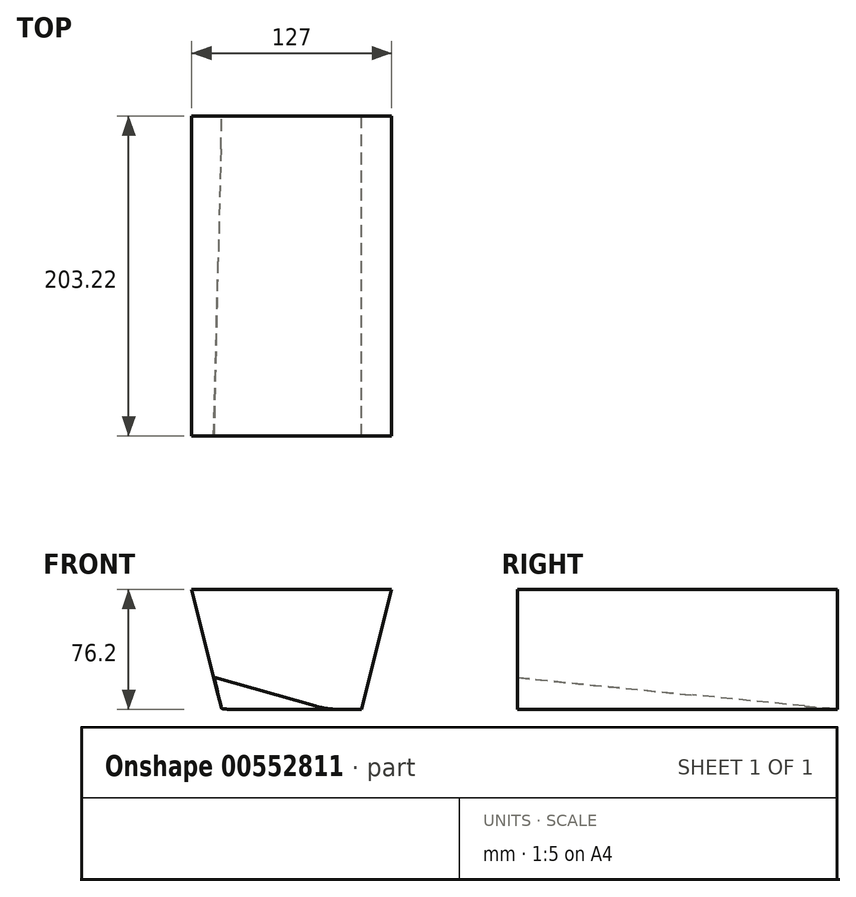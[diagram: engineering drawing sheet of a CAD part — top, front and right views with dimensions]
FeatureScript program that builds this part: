
annotation { "Feature Type Name" : "Feature", "Feature Type Description" : "" }
export const myFeature = defineFeature(function(context is Context, id is Id, definition is map)
    precondition{}
    {
        {
            var Q0;
            Q0=qCreatedBy(makeId("Front.planeOp"),FACE);
            var sketch = newSketch(context, id + "F0", { "sketchPlane" : qUnion([Q0])});
            skLineSegment(sketch, "E0.bottom", {"start": v(63.5, -38.1) * mm, "end": v(-63.5, -38.1) * mm});
            skLineSegment(sketch, "E0.top", {"start": v(63.5, 38.1) * mm, "end": v(-63.5, 38.1) * mm});
            skLineSegment(sketch, "E0.left", {"start": v(63.5, -38.1) * mm, "end": v(63.5, 38.1) * mm});
            skLineSegment(sketch, "E0.right", {"start": v(-63.5, -38.1) * mm, "end": v(-63.5, 38.1) * mm});
            skPoint(sketch, "E0.middle", {"position": v(0, 0) * mm});
            skLineSegment(sketch, "E1", {"start": v(-63.5, 38.1) * mm, "end": v(-44.45, -38.1) * mm});
            skLineSegment(sketch, "E2", {"start": v(0, 38.1) * mm, "end": v(0, -38.1) * mm, "construction": true});
            skLineSegment(sketch, "E3.MirrorCS", {"start": v(63.5, 38.1) * mm, "end": v(44.45, -38.1) * mm});
            skSolve(sketch);
        }
        {
            var Q0;
            Q0=makeQuery(id+"F0.imprint","IMPRINT",FACE,{"disambiguationData":[TD([[makeQuery(id+"F0.imprint","IMPRINT",EDGE,{"derivedFrom":sQuery(id+"F0.wireOp",EDGE,"E0.top")}),1.0]])]});
            extrude(context, id + "F1", {"entities" : qUnion([Q0]), "depth" : 203.2 * mm, "offsetDistance" : 25.4 * mm});
        }
        {
            var Q0;
            Q0=makeQuery(id+"F1.opExtrude","CAP_FACE",FACE,{"disambiguationData":[OSD([sQuery(id+"F0.wireOp",EDGE,"E0.bottom"),sQuery(id+"F0.wireOp",EDGE,"E0.top"),sQuery(id+"F0.wireOp",EDGE,"E1"),sQuery(id+"F0.wireOp",EDGE,"E3.MirrorCS")])],"isStart":false});
            var sketch = newSketch(context, id + "F2", { "sketchPlane" : qUnion([Q0])});
            skLineSegment(sketch, "E4", {"start": v(-49.53, -17.78) * mm, "end": v(-44.45, -38.1) * mm});
            skLineSegment(sketch, "E5", {"start": v(-44.45, -38.1) * mm, "end": v(0, -38.1) * mm});
            skLineSegment(sketch, "E6", {"start": v(0, -38.1) * mm, "end": v(0, -31.75) * mm});
            skLineSegment(sketch, "E7", {"start": v(0, -31.75) * mm, "end": v(-49.53, -17.78) * mm});
            skSolve(sketch);
        }
        {
            var Q0;
            Q0=sQuery(id+"F2.wireOp",VERTEX,"E7.start");
            var Q1;
            Q1=sQuery(id+"F2.wireOp",VERTEX,"E4.start");
            var Q2;
            Q2=makeQuery(id+"F1.opExtrude","CAP_VERTEX",VERTEX,{"disambiguationData":[OSD([sQuery(id+"F0.wireOp",EDGE,"E0.bottom"),sQuery(id+"F0.wireOp",EDGE,"E1")])],"isStart":true});
            cPlane(context, id + "F3", {"entities" : qUnion([Q0, Q1, Q2]), "cplaneType" : CPlaneType.THREE_POINT, "offset" : 25.4 * mm, "width" : 152.4 * mm, "height" : 152.4 * mm});
        }
        {
            var Q0;
            Q0=qCreatedBy(id+"F3.planeOp",FACE);
            var sketch = newSketch(context, id + "F4", { "sketchPlane" : qUnion([Q0])});
            skLineSegment(sketch, "E8", {"start": v(-37.81, -200.68) * mm, "end": v(-32.54, 3.53) * mm});
            skLineSegment(sketch, "E9", {"start": v(-37.81, -200.68) * mm, "end": v(83.29, -203.81) * mm});
            skLineSegment(sketch, "E10", {"start": v(-32.54, 3.53) * mm, "end": v(83.29, 0.53) * mm});
            skLineSegment(sketch, "E11", {"start": v(83.29, 0.53) * mm, "end": v(83.29, -203.81) * mm});
            skSolve(sketch);
        }
        {
            var Q0;
            Q0 = qSketchRegion(id + "F4", true);
            extrude(context, id + "F5", {"entities" : qUnion([Q0]), "operationType" : NewBodyOperationType.REMOVE, "endBound" : BoundingType.THROUGH_ALL, "oppositeDirection" : true, "depth" : 25.4 * mm, "offsetDistance" : 25.4 * mm});
        }
        {
            var Q0;
            {var subQ0=sQuery(id+"F4.wireOp",EDGE,"E11");var subQ1=sQuery(id+"F4.wireOp",EDGE,"E10");var subQ2=sQuery(id+"F4.wireOp",EDGE,"E9");var subQ3=sQuery(id+"F4.wireOp",EDGE,"E8");Q0=makeQuery(id+"F4tuMMxzGeYJKgA_1.1.F5.boolean.opBoolean","INTERSECT",EDGE,{"derivedFrom":[makeQuery(id+"F5.boolean.opBoolean","COPY",FACE,{"derivedFrom":makeQuery(id+"F5.opExtrude","CAP_FACE",FACE,{"disambiguationData":[OSD([subQ3,subQ2,subQ1,subQ0])],"isStart":true})}),makeQuery(id+"F4tuMMxzGeYJKgA_1.1.F5.opExtrude","CAP_FACE",FACE,{"disambiguationData":[OSD([subQ3,subQ2,subQ1,subQ0])],"isStart":true})]});}
            var Q1;
            Q1=makeQuery(id+"F5.boolean.opBoolean","INTERSECT",EDGE,{"derivedFrom":[makeQuery(id+"F1.opExtrude","SWEPT_FACE",FACE,{"disambiguationData":[OSD([sQuery(id+"F0.wireOp",EDGE,"E0.bottom")])]}),makeQuery(id+"F5.opExtrude","CAP_FACE",FACE,{"disambiguationData":[OSD([sQuery(id+"F4.wireOp",EDGE,"E8"),sQuery(id+"F4.wireOp",EDGE,"E9"),sQuery(id+"F4.wireOp",EDGE,"E10"),sQuery(id+"F4.wireOp",EDGE,"E11")])],"isStart":true})]});
            var Q2;
            Q2=makeQuery(id+"F4tuMMxzGeYJKgA_1.1.F5.boolean.opBoolean","INTERSECT",EDGE,{"derivedFrom":[makeQuery(id+"F1.opExtrude","SWEPT_FACE",FACE,{"disambiguationData":[OSD([sQuery(id+"F0.wireOp",EDGE,"E0.bottom")])]}),makeQuery(id+"F4tuMMxzGeYJKgA_1.1.F5.opExtrude","CAP_FACE",FACE,{"disambiguationData":[OSD([sQuery(id+"F4.wireOp",EDGE,"E8"),sQuery(id+"F4.wireOp",EDGE,"E9"),sQuery(id+"F4.wireOp",EDGE,"E10"),sQuery(id+"F4.wireOp",EDGE,"E11")])],"isStart":true})]});
            fillet(context, id + "F6", {"entities" : qUnion([Q0, Q1, Q2]), "radius" : 50.8 * mm, "tangentPropagation" : true, "allowEdgeOverflow" : false});
        }
        {
            var Q0;
            Q0=makeQuery(id+"F4tuMMxzGeYJKgA_1.1.F5.boolean.opBoolean","COPY",EDGE,{"derivedFrom":makeQuery(id+"F4tuMMxzGeYJKgA_1.1.F5.opExtrude","CAP_EDGE",EDGE,{"disambiguationData":[OSD([sQuery(id+"F4.wireOp",EDGE,"E8")])],"isStart":true})});
            var Q1;
            Q1=makeQuery(id+"F5.boolean.opBoolean","COPY",EDGE,{"derivedFrom":makeQuery(id+"F5.opExtrude","CAP_EDGE",EDGE,{"disambiguationData":[OSD([sQuery(id+"F4.wireOp",EDGE,"E8")])],"isStart":true})});
            fillet(context, id + "F7", {"entities" : qUnion([Q0, Q1]), "radius" : 12.7 * mm, "tangentPropagation" : true, "allowEdgeOverflow" : false});
        }
    });
